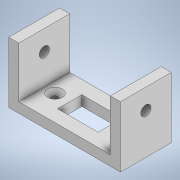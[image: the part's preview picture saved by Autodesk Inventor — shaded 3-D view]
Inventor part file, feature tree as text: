
AUTODESK INVENTOR PART (.ipt)
format: ipt  version: 2022 (Build 260153000, 153)  size: 148,992 bytes
history: native  units: mm
features: extrude x5, sketch x5
ambient origin geometry x8: Origin, YZ Plane, XZ Plane, XY Plane, X Axis, Y Axis, Z Axis, Center Point
bodies: Solid1 (feature_tree)
feature tree (10):
  extrude  "Extrusion1"  Depth=30.0mm
  extrude  "Extrusion2"  Depth=25.0mm
  extrude  "Extrusion3"  Depth=25.0mm
  extrude  "Extrusion4"  Depth=25.0mm TaperAngle=0.0deg
  extrude  "Extrusion5"  Depth=10.0mm
  sketch  "Sketch1"  dims[d0=55.0mm d1=30.0mm]
  sketch  "Sketch2"  dims[d2=5.0mm d3=25.0mm]
  sketch  "Sketch3"  dims[d4=45.0mm d5=25.0mm]
  sketch  "Sketch4"  dims[d6=5.0mm d7=25.0mm d8=0.0mm]
  sketch  "Sketch5"  dims[d9=5.0mm d10=10.0mm d11=12.5mm d12=0.0mm d13=0.0mm d14=20.0mm d15=12.0mm d16=12.5mm d17=22.5mm d18=0.0mm d19=0.0mm d20=7.25mm d21=7.25mm d22=5.25mm d23=5.25mm d24=12.5mm d25=12.5mm d26=2.1735mm d27=-7.853982mm d28=2.903mm d29=2.903mm d30=5.25mm d31=0.0mm d32=0.0mm]
